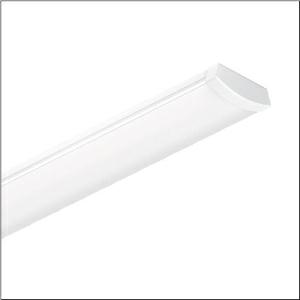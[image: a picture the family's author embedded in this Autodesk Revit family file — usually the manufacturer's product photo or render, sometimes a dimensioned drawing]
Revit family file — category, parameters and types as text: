
# Revit family: siluette_r__21_51ln12mkm40a_b89c
name_source: partatom
category: Lighting Fixtures
units: mm (PartAtom-declared; Revit-internal decimal feet)

## family parameters
Cut with Voids When Loaded = No
Host = Face
Light Source = No
Part Type = Normal
Room Calculation Point = No
Round Connector Dimension = Use Diameter
Shared = No

## types (1)
- --- (1 x LED, 2980 lm, 20.6 W, 5000K)
    Apparent Load = 21 VA
    CIE Flux Codes = 43 73 92 94 100
    Color Rendering = 80
    Color Temperature = 5000K
    Default Elevation = 1800 mm
    Description = Siluette® 21, office luminaire, primary optical cover: enclosure, of PC, frosted, light emission: direct distribution, primary light characteristic: symmetric, installation type: suspended mounting, surface-mounted, LED, rated luminous flux: 4.800lm, luminous efficacy: 135lm/W, light colour: 830/840/850, colour temperature: 3000/4000/5000K, with terminal, 3-pole, mains connection: 220..240V, AC, 50/60Hz, rated input power: 35W, housing, of sheet steel, white, length: 1.200mm, width: 152mm, height: 53mm, end cap, of PMMA, white, protection rating (complete): IP44, insulation class (complete): insulation class I (protective earthing), certification: CE, UKCA, protection symbol: D, permissible operating ambient temperature: -20..+40°C, contact your sales advisor before using the luminaires in applications with unclear chemical exposure, large temperature fluctuations or condensation-forming humidity, corresponds to IFS (International Featured Standards) requirements for safety and quality in the food industry, packaging unit: 1 piece
    Height = 52 mm  [stored 0.170604 ft]
    Lamp = 1 x LED
    Lamp Light Flux = 2980 lm
    Lamp Power = 20.6 W
    Lamp count = 1
    Length = 1185 mm
    Luminous efficacy = 145 lm/W
    Manufacturer = Siteco
    ModVariant = No
    Model = 51LN12MKM40A
    Mounting Place = Ceiling
    Mounting Type = Pendant
    Number of Poles = 1
    OnlyDefault = Yes
    Power Factor = 1
    Product Name = Siluette® 21
    Product group = office luminaire | ceiling pendant
    ProductGroupID = 902
    Protection Class = Protection class I
    Protection Degree = IP 44
    RLX_Detail_Level = 1
    RLX_Emergency_Light_Flux = 0 lm
    RLX_Emergency_Type = 0
    RLX_Emergency_Type_DB = No
    RlxData = <blob elided: 20241 chars, md5=1ec31a9e>
    Socket = socket
    Standby Power = 0 W
    System Light Flux = 2980 lm
    System Power = 21 W
    Type Comments = individual setting: colour temperature 5000K, luminous flux: 60 % | (OFF | OFF | ON) | 200 mA
    Type Image = l_1296910.jpg
    URL = http://relux.com
    VarID = @adj_001859
    Voltage = 0 V
    Weight = 0.00 kg
    Width = 152 mm

note: [stored X ft] marks values corroborated as IEEE doubles in the binary element streams (Revit-internal decimal feet)

## geometry (parser evidence)
native form markers: Blend x4, Sweep x12
no freeform markers — native parametric forms only
